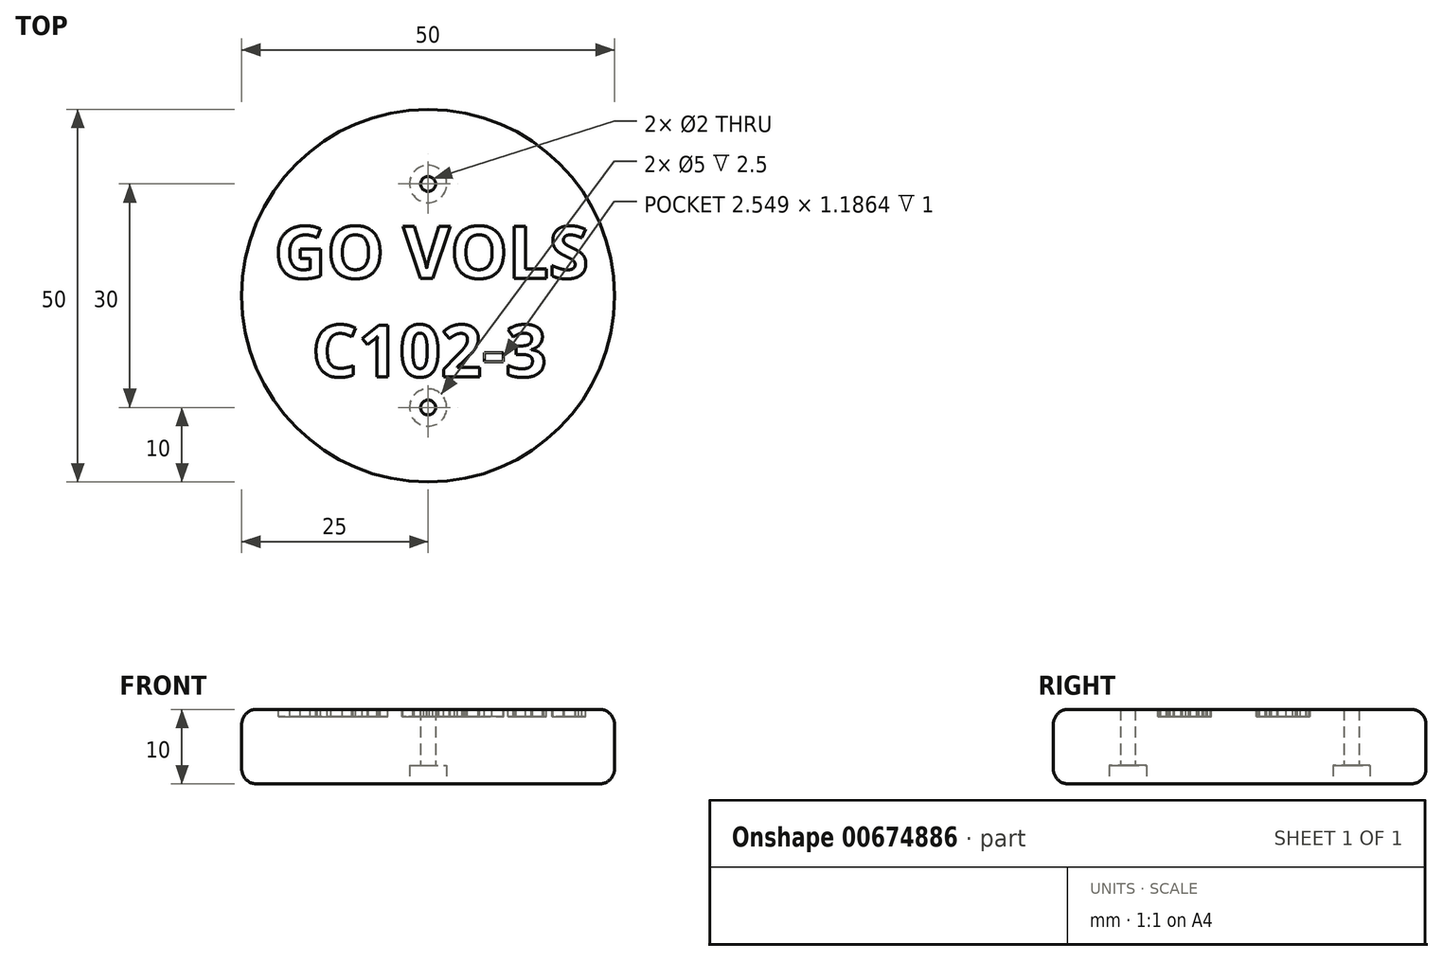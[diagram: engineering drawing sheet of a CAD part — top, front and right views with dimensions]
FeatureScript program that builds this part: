
annotation { "Feature Type Name" : "Feature", "Feature Type Description" : "" }
export const myFeature = defineFeature(function(context is Context, id is Id, definition is map)
    precondition{}
    {
        {
            var Q0;
            Q0=qCreatedBy(makeId("Top.planeOp"),FACE);
            var sketch = newSketch(context, id + "F0", { "sketchPlane" : qUnion([Q0])});
            skCircle(sketch, "E0", {"center": v(0, 0) * mm, "radius": 25 * mm});
            skSolve(sketch);
        }
        {
            var Q0;
            Q0=qSketchRegion(id+"F0",true);
            extrude(context, id + "F1", {"entities" : qUnion([Q0]), "depth" : 10 * mm});
        }
        {
            var Q0;
            Q0=makeQuery(id+"F1.opExtrude","CAP_FACE",FACE,{"disambiguationData":[OSD([sQuery(id+"F0.wireOp",EDGE,"E0")])],"isStart":false});
            var sketch = newSketch(context, id + "F2", { "sketchPlane" : qUnion([Q0])});
            skText(sketch, "E1", { "text": " GO VOLS \n   C102-3", "fontName": "OpenSans-Bold.ttf"});
            const initialGuessF2  = {"E1": [-0.02318, 0.00235, 1, 0, 0.007]};
            skSetInitialGuess(sketch, initialGuessF2);
            skSolve(sketch);
        }
        {
            var Q0;
            Q0=qSketchRegion(id+"F2",true);
            extrude(context, id + "F3", {"entities" : qUnion([Q0]), "operationType" : NewBodyOperationType.REMOVE, "oppositeDirection" : true, "depth" : 1 * mm});
        }
        {
            var Q0;
            Q0=makeQuery(id+"F1.opExtrude","CAP_EDGE",EDGE,{"disambiguationData":[OSD([sQuery(id+"F0.wireOp",EDGE,"E0")])],"isStart":false});
            var Q1;
            Q1=makeQuery(id+"F1.opExtrude","CAP_EDGE",EDGE,{"disambiguationData":[OSD([sQuery(id+"F0.wireOp",EDGE,"E0")])],"isStart":true});
            fillet(context, id + "F4", {"entities" : qUnion([Q0, Q1]), "radius" : 2 * mm, "tangentPropagation" : true, "allowEdgeOverflow" : false});
        }
        {
            var Q0;
            Q0=makeQuery(id+"F1.opExtrude","CAP_FACE",FACE,{"disambiguationData":[OSD([sQuery(id+"F0.wireOp",EDGE,"E0")])],"isStart":true});
            var sketch = newSketch(context, id + "F5", { "sketchPlane" : qUnion([Q0])});
            skPoint(sketch, "E2", {"position": v(0, 15) * mm});
            skPoint(sketch, "E3", {"position": v(0, -15) * mm});
            skSolve(sketch);
        }
        {
            var Q0;
            Q0=sQuery(id+"F5.wireOp",VERTEX,"E2");
            var Q1;
            Q1=sQuery(id+"F5.wireOp",VERTEX,"E3");
            var Q2;
            Q2=makeQuery(id+"F1.opExtrude","SWEPT_BODY",BODY,{"disambiguationData":[OSD([sQuery(id+"F0.wireOp",EDGE,"E0")])]});
            hole(context, id + "F6", {"style" : HoleStyle.C_BORE, "endStyle" : HoleEndStyle.THROUGH, "holeDiameter" : 2 * mm, "cBoreDiameter" : 5 * mm, "cBoreDepth" : 2.5 * mm, "startFromSketch" : true, "locations" : qUnion([Q0, Q1]), "scope" : qUnion([Q2]), "isTappedThrough" : true});
        }
    });
